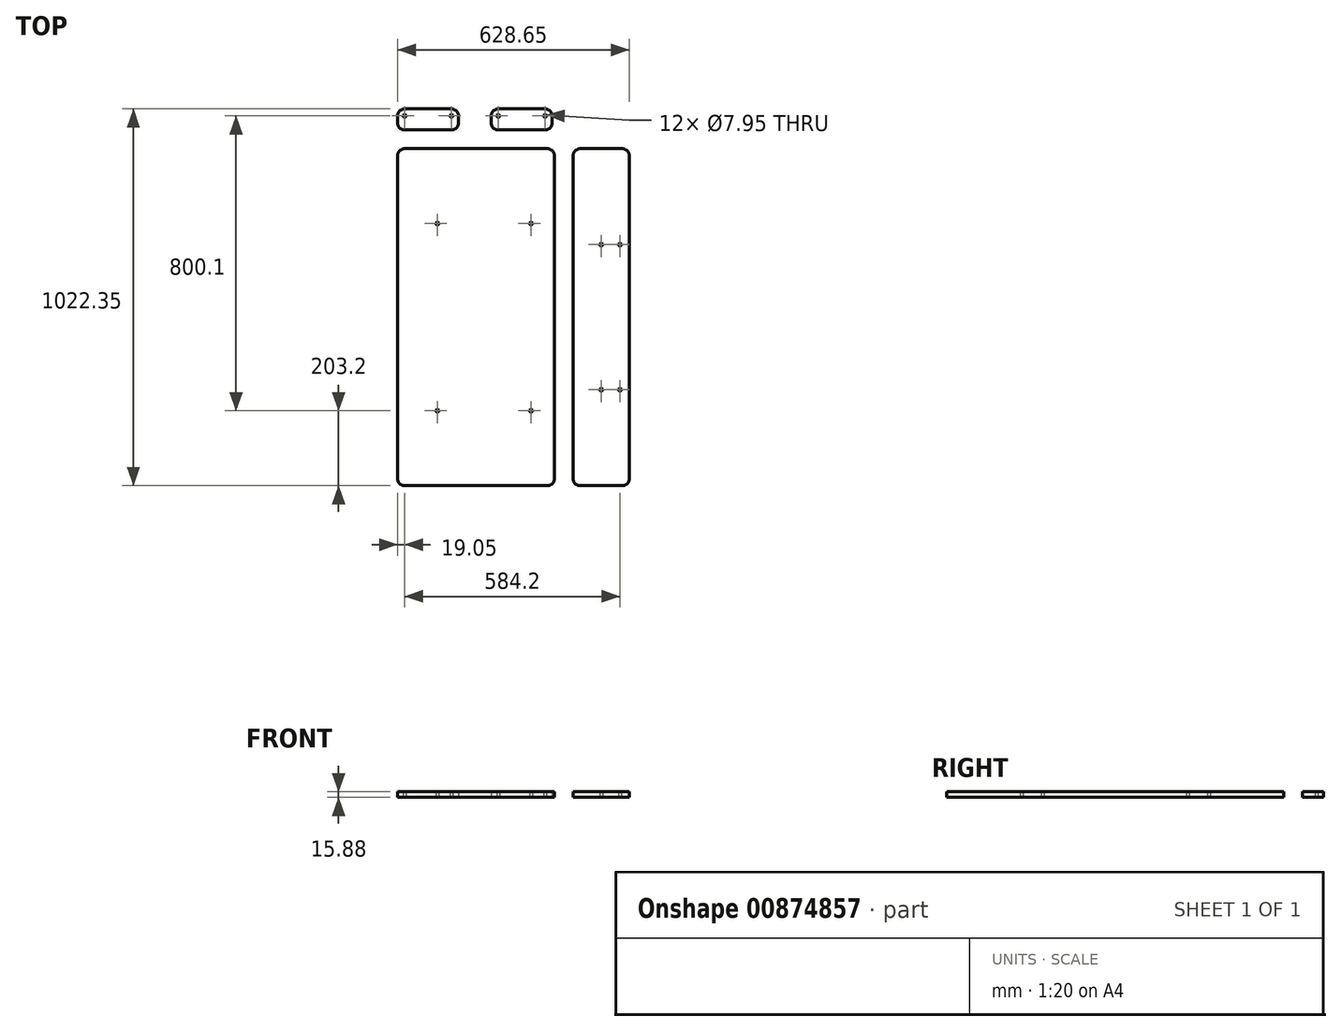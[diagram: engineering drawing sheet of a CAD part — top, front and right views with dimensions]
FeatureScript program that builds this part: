
annotation { "Feature Type Name" : "Feature", "Feature Type Description" : "" }
export const myFeature = defineFeature(function(context is Context, id is Id, definition is map)
    precondition{}
    {
        {
            var Q0;
            Q0=qCreatedBy(makeId("Top.planeOp"),FACE);
            var sketch = newSketch(context, id + "F0", { "sketchPlane" : qUnion([Q0])});
            skLineSegment(sketch, "E0.bottom", {"start": v(19.05, 0) * mm, "end": v(406.4, 0) * mm});
            skLineSegment(sketch, "E0.top", {"start": v(19.05, 914.4) * mm, "end": v(406.4, 914.4) * mm});
            skLineSegment(sketch, "E0.left", {"start": v(0, 19.05) * mm, "end": v(0, 895.35) * mm});
            skLineSegment(sketch, "E0.right", {"start": v(425.45, 19.05) * mm, "end": v(425.45, 895.35) * mm});
            skPoint(sketch, "E1.visualSharp", {"position": v(0, 914.4) * mm});
            skArc(sketch, "E1.filletArc", {"start": v(19.05, 914.4) * mm, "mid": v(5.58, 908.82) * mm, "end": v(0, 895.35) * mm});
            skPoint(sketch, "E2.visualSharp", {"position": v(425.45, 914.4) * mm});
            skArc(sketch, "E2.filletArc", {"start": v(425.45, 895.35) * mm, "mid": v(419.87, 908.82) * mm, "end": v(406.4, 914.4) * mm});
            skPoint(sketch, "E3.visualSharp", {"position": v(425.45, 0) * mm});
            skArc(sketch, "E3.filletArc", {"start": v(406.4, 0) * mm, "mid": v(419.87, 5.58) * mm, "end": v(425.45, 19.05) * mm});
            skPoint(sketch, "E4.visualSharp", {"position": v(0, 0) * mm});
            skArc(sketch, "E4.filletArc", {"start": v(0, 19.05) * mm, "mid": v(5.58, 5.58) * mm, "end": v(19.05, 0) * mm});
            skCircle(sketch, "E5", {"center": v(107.95, 711.2) * mm, "radius": 3.98 * mm});
            skCircle(sketch, "E6", {"center": v(361.95, 711.2) * mm, "radius": 3.98 * mm});
            skCircle(sketch, "E7", {"center": v(361.95, 203.2) * mm, "radius": 3.98 * mm});
            skCircle(sketch, "E8", {"center": v(107.95, 203.2) * mm, "radius": 3.98 * mm});
            skLineSegment(sketch, "E9.bottom", {"start": v(495.3, 0) * mm, "end": v(609.6, 0) * mm});
            skLineSegment(sketch, "E9.top", {"start": v(495.3, 914.4) * mm, "end": v(609.6, 914.4) * mm});
            skLineSegment(sketch, "E9.left", {"start": v(476.25, 19.05) * mm, "end": v(476.25, 895.35) * mm});
            skLineSegment(sketch, "E9.right", {"start": v(628.65, 19.05) * mm, "end": v(628.65, 895.35) * mm});
            skPoint(sketch, "E10.visualSharp", {"position": v(476.25, 0) * mm});
            skArc(sketch, "E10.filletArc", {"start": v(476.25, 19.05) * mm, "mid": v(481.83, 5.58) * mm, "end": v(495.3, 0) * mm});
            skPoint(sketch, "E11.visualSharp", {"position": v(628.65, 0) * mm});
            skArc(sketch, "E11.filletArc", {"start": v(609.6, 0) * mm, "mid": v(623.07, 5.58) * mm, "end": v(628.65, 19.05) * mm});
            skPoint(sketch, "E12.visualSharp", {"position": v(628.65, 914.4) * mm});
            skArc(sketch, "E12.filletArc", {"start": v(628.65, 895.35) * mm, "mid": v(623.07, 908.82) * mm, "end": v(609.6, 914.4) * mm});
            skPoint(sketch, "E13.visualSharp", {"position": v(476.25, 914.4) * mm});
            skArc(sketch, "E13.filletArc", {"start": v(495.3, 914.4) * mm, "mid": v(481.83, 908.82) * mm, "end": v(476.25, 895.35) * mm});
            skCircle(sketch, "E14", {"center": v(552.45, 260.35) * mm, "radius": 3.98 * mm});
            skCircle(sketch, "E15", {"center": v(603.25, 260.35) * mm, "radius": 3.98 * mm});
            skCircle(sketch, "E16", {"center": v(603.25, 654.05) * mm, "radius": 3.98 * mm});
            skCircle(sketch, "E17", {"center": v(552.45, 654.05) * mm, "radius": 3.98 * mm});
            skLineSegment(sketch, "E18.bottom", {"start": v(19.05, 965.2) * mm, "end": v(146.05, 965.2) * mm});
            skLineSegment(sketch, "E18.top", {"start": v(19.05, 1022.35) * mm, "end": v(146.05, 1022.35) * mm});
            skLineSegment(sketch, "E18.left", {"start": v(0, 984.25) * mm, "end": v(0, 1003.3) * mm});
            skLineSegment(sketch, "E18.right", {"start": v(165.1, 984.25) * mm, "end": v(165.1, 1003.3) * mm});
            skPoint(sketch, "E19.visualSharp", {"position": v(0, 1022.35) * mm});
            skArc(sketch, "E19.filletArc", {"start": v(19.05, 1022.35) * mm, "mid": v(5.58, 1016.77) * mm, "end": v(0, 1003.3) * mm});
            skPoint(sketch, "E20.visualSharp", {"position": v(0, 965.2) * mm});
            skArc(sketch, "E20.filletArc", {"start": v(0, 984.25) * mm, "mid": v(5.58, 970.78) * mm, "end": v(19.05, 965.2) * mm});
            skPoint(sketch, "E21.visualSharp", {"position": v(165.1, 965.2) * mm});
            skArc(sketch, "E21.filletArc", {"start": v(146.05, 965.2) * mm, "mid": v(159.52, 970.78) * mm, "end": v(165.1, 984.25) * mm});
            skPoint(sketch, "E22.visualSharp", {"position": v(165.1, 1022.35) * mm});
            skArc(sketch, "E22.filletArc", {"start": v(165.1, 1003.3) * mm, "mid": v(159.52, 1016.77) * mm, "end": v(146.05, 1022.35) * mm});
            skCircle(sketch, "E23", {"center": v(19.05, 1003.3) * mm, "radius": 3.98 * mm});
            skCircle(sketch, "E24", {"center": v(146.05, 1003.3) * mm, "radius": 3.98 * mm});
            skArc(sketch, "E25.1.0.0", {"start": v(273.05, 1022.35) * mm, "mid": v(259.58, 1016.77) * mm, "end": v(254, 1003.3) * mm});
            skArc(sketch, "E25.1.0.1", {"start": v(419.1, 1003.3) * mm, "mid": v(413.52, 1016.77) * mm, "end": v(400.05, 1022.35) * mm});
            skPoint(sketch, "E25.1.0.2", {"position": v(254, 965.2) * mm});
            skArc(sketch, "E25.1.0.3", {"start": v(254, 984.25) * mm, "mid": v(259.58, 970.78) * mm, "end": v(273.05, 965.2) * mm});
            skLineSegment(sketch, "E25.1.0.4", {"start": v(273.05, 965.2) * mm, "end": v(400.05, 965.2) * mm});
            skPoint(sketch, "E25.1.0.5", {"position": v(254, 914.4) * mm});
            skPoint(sketch, "E25.1.0.6", {"position": v(419.1, 965.2) * mm});
            skPoint(sketch, "E25.1.0.7", {"position": v(254, 1022.35) * mm});
            skLineSegment(sketch, "E25.1.0.8", {"start": v(273.05, 1022.35) * mm, "end": v(400.05, 1022.35) * mm});
            skArc(sketch, "E25.1.0.9", {"start": v(400.05, 965.2) * mm, "mid": v(413.52, 970.78) * mm, "end": v(419.1, 984.25) * mm});
            skPoint(sketch, "E25.1.0.10", {"position": v(419.1, 1022.35) * mm});
            skCircle(sketch, "E25.1.0.11", {"center": v(273.05, 1003.3) * mm, "radius": 3.98 * mm});
            skCircle(sketch, "E25.1.0.12", {"center": v(400.05, 1003.3) * mm, "radius": 3.98 * mm});
            skLineSegment(sketch, "E25.1.0.13", {"start": v(254, 984.25) * mm, "end": v(254, 1003.3) * mm});
            skLineSegment(sketch, "E25.1.0.14", {"start": v(419.1, 984.25) * mm, "end": v(419.1, 1003.3) * mm});
            skLineSegment(sketch, "E25.direction1", {"start": v(0, 914.4) * mm, "end": v(254, 914.4) * mm, "construction": true});
            skSolve(sketch);
        }
        {
            var Q0;
            Q0 = qSketchRegion(id + "F0", true);
            extrude(context, id + "F1", {"entities" : qUnion([Q0]), "flatOperationType" : FlatOperationType.REMOVE, "depth" : 15.88 * mm, "offsetDistance" : 25.4 * mm, "domain" : OperationDomain.MODEL});
        }
    });
